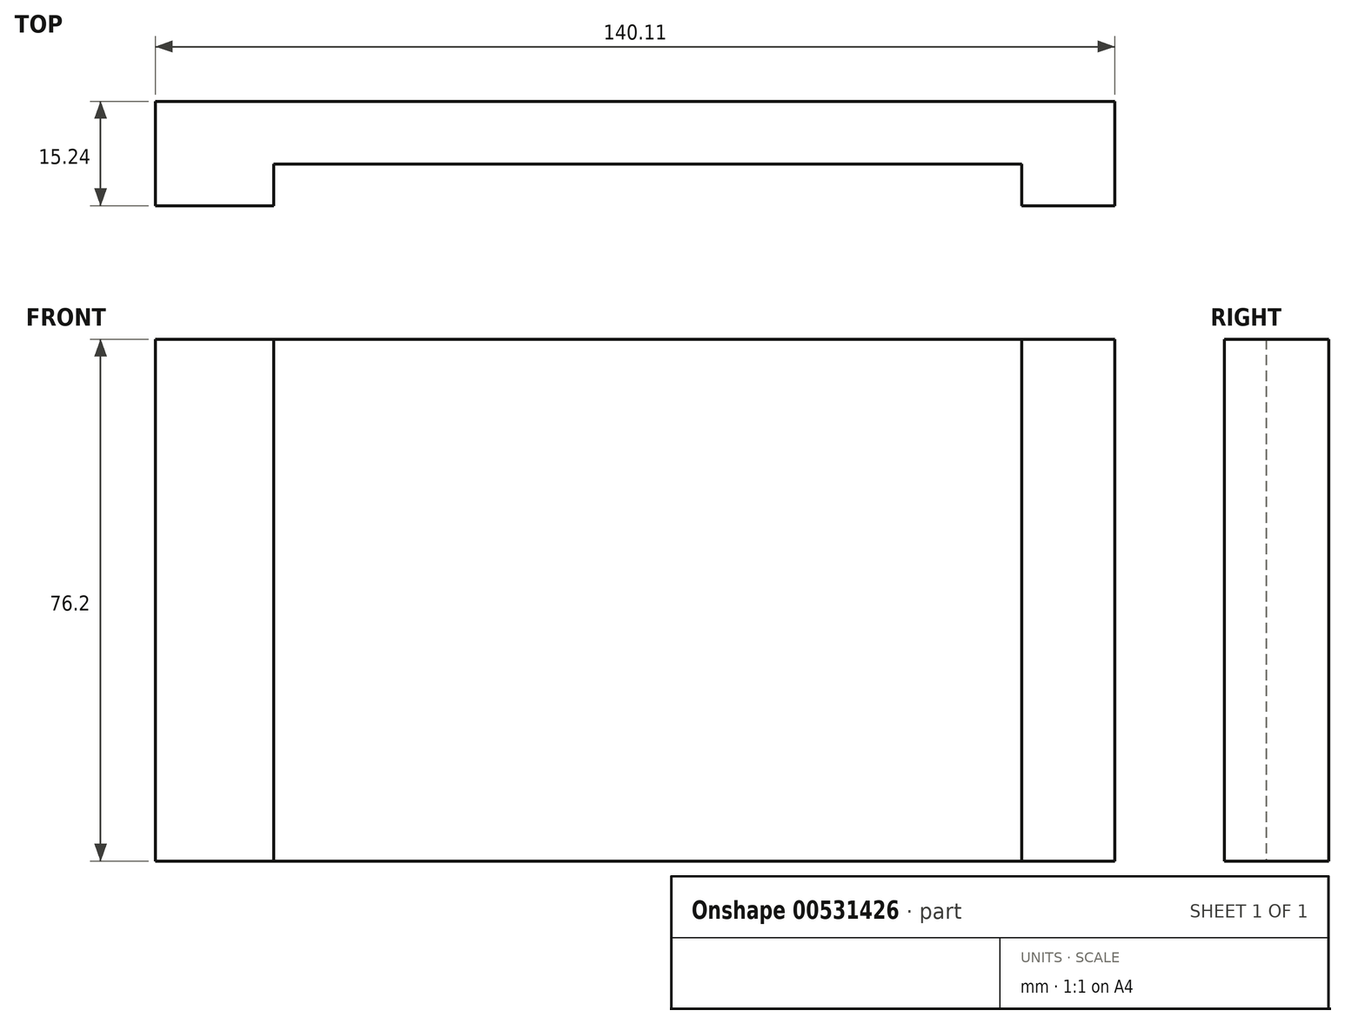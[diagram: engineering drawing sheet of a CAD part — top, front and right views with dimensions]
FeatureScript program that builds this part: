
annotation { "Feature Type Name" : "Feature", "Feature Type Description" : "" }
export const myFeature = defineFeature(function(context is Context, id is Id, definition is map)
    precondition{}
    {
        {
            var Q0;
            Q0=qCreatedBy(makeId("Top.planeOp"),FACE);
            var sketch = newSketch(context, id + "F0", { "sketchPlane" : qUnion([Q0])});
            skLineSegment(sketch, "E0", {"start": v(0, 0) * mm, "end": v(140.1, 0) * mm});
            skLineSegment(sketch, "E1", {"start": v(140.1, 0) * mm, "end": v(140.1, -15.24) * mm});
            skLineSegment(sketch, "E2", {"start": v(140.1, -15.24) * mm, "end": v(126.5, -15.24) * mm});
            skLineSegment(sketch, "E3", {"start": v(126.5, -15.24) * mm, "end": v(126.5, -9.14) * mm});
            skLineSegment(sketch, "E4", {"start": v(126.5, -9.14) * mm, "end": v(17.27, -9.14) * mm});
            skLineSegment(sketch, "E5", {"start": v(17.27, -9.14) * mm, "end": v(17.27, -15.24) * mm});
            skLineSegment(sketch, "E6", {"start": v(17.27, -15.24) * mm, "end": v(0, -15.24) * mm});
            skLineSegment(sketch, "E7", {"start": v(0, -15.24) * mm, "end": v(0, 0) * mm});
            skSolve(sketch);
        }
        {
            var Q0;
            Q0=makeQuery(id+"F0.imprint","IMPRINT",FACE,{"disambiguationData":[TD([[makeQuery(id+"F0.imprint","IMPRINT",EDGE,{"derivedFrom":sQuery(id+"F0.wireOp",EDGE,"E0")}),-1.0]])]});
            extrude(context, id + "F1", {"entities" : qUnion([Q0]), "depth" : 76.2 * mm, "offsetDistance" : 25.4 * mm});
        }
    });
